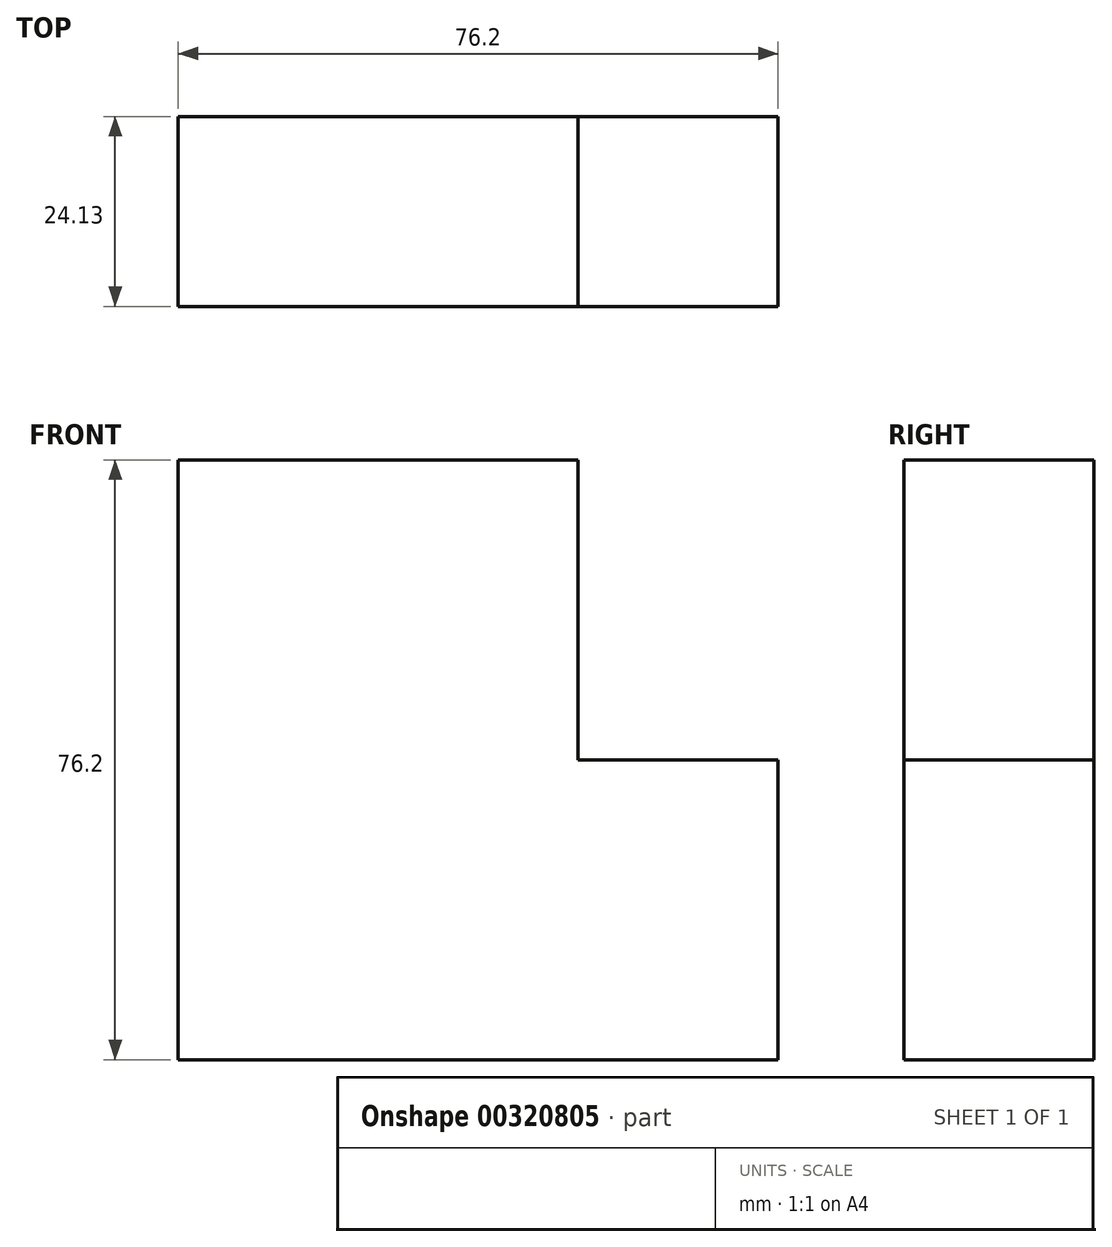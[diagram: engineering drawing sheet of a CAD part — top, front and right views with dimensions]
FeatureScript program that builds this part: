
annotation { "Feature Type Name" : "Feature", "Feature Type Description" : "" }
export const myFeature = defineFeature(function(context is Context, id is Id, definition is map)
    precondition{}
    {
        {
            var Q0;
            Q0=qCreatedBy(makeId("Front.planeOp"),FACE);
            var sketch = newSketch(context, id + "F0", { "sketchPlane" : qUnion([Q0])});
            skLineSegment(sketch, "E0.bottom", {"start": v(-16.17, -30.54) * mm, "end": v(21.93, -30.54) * mm});
            skLineSegment(sketch, "E0.top", {"start": v(-16.17, -55.94) * mm, "end": v(21.93, -55.94) * mm});
            skLineSegment(sketch, "E0.left", {"start": v(-16.17, -30.54) * mm, "end": v(-16.17, -55.94) * mm});
            skLineSegment(sketch, "E0.right", {"start": v(21.93, -30.54) * mm, "end": v(21.93, -55.94) * mm});
            skLineSegment(sketch, "E1", {"start": v(-16.17, -30.54) * mm, "end": v(-16.17, 20.26) * mm});
            skLineSegment(sketch, "E2", {"start": v(-16.17, 20.26) * mm, "end": v(34.63, 20.26) * mm});
            skLineSegment(sketch, "E3", {"start": v(34.63, 20.26) * mm, "end": v(34.63, -17.84) * mm});
            skLineSegment(sketch, "E4", {"start": v(34.63, -17.84) * mm, "end": v(60.03, -17.84) * mm});
            skLineSegment(sketch, "E5", {"start": v(60.03, -17.84) * mm, "end": v(60.03, -55.94) * mm});
            skLineSegment(sketch, "E6", {"start": v(21.93, -55.94) * mm, "end": v(60.03, -55.94) * mm});
            skSolve(sketch);
        }
        {
            var Q0;
            Q0=makeQuery(id+"F0.imprint","IMPRINT",FACE,{"disambiguationData":[TD([[makeQuery(id+"F0.imprint","IMPRINT",EDGE,{"derivedFrom":sQuery(id+"F0.wireOp",EDGE,"E0.bottom")}),-1.0]])]});
            var Q1;
            Q1=makeQuery(id+"F0.imprint","IMPRINT",FACE,{"disambiguationData":[TD([[makeQuery(id+"F0.imprint","IMPRINT",EDGE,{"derivedFrom":sQuery(id+"F0.wireOp",EDGE,"E0.bottom")}),1.0]])]});
            extrude(context, id + "F1", {"entities" : qUnion([Q0, Q1]), "depth" : 24.13 * mm});
        }
    });
